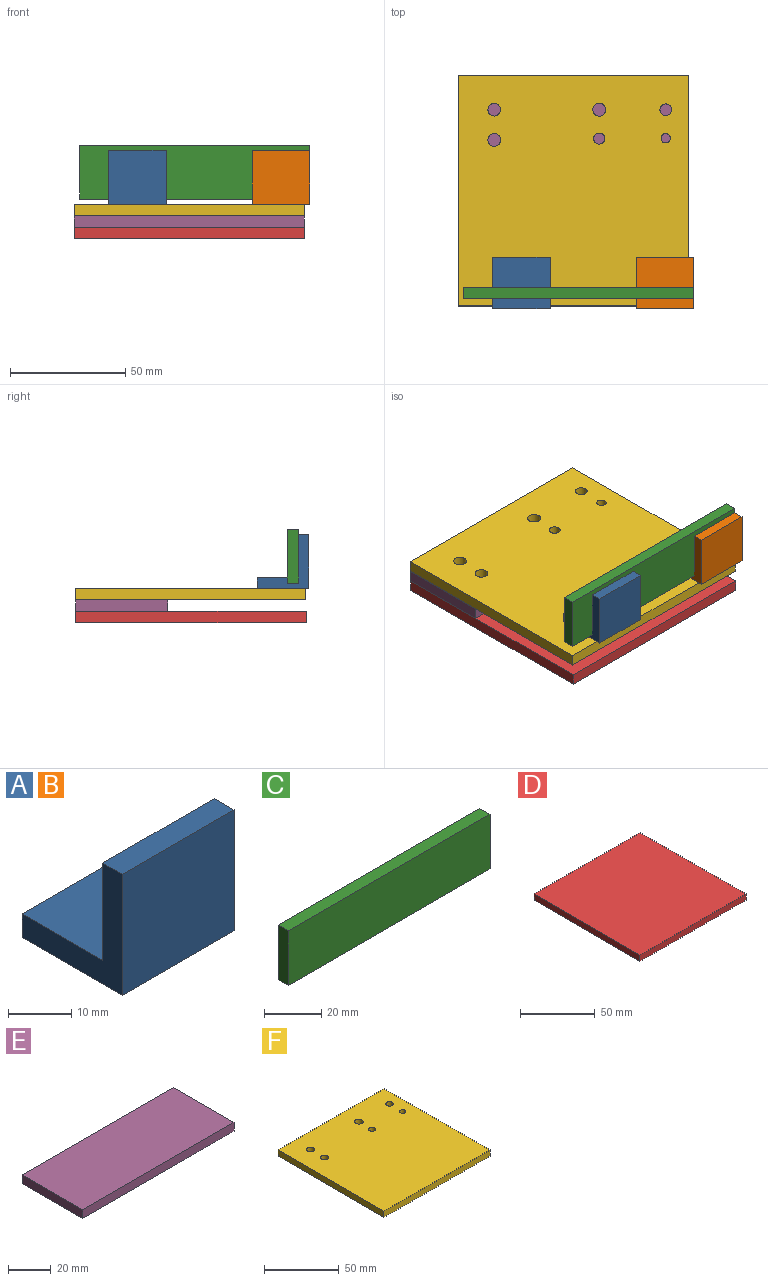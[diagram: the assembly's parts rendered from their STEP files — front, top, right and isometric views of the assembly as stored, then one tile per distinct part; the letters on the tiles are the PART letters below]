
ASSEMBLY  parts=6 mates=5
PART A: 8 faces, bbox 25x22.5x23.5 mm
  f0: plane 25x4.41mm, normal (0,0,1), area 110.2mm2, adj f1,f5,f6,f7
  f1: plane 25x23.47mm, normal (0,-1,0), area 586.8mm2, adj f0,f2,f6,f7
  f2: plane 25x22.48mm, normal (0,0,-1), area 562.1mm2, adj f1,f3,f6,f7
  f3: plane 25x4.58mm, normal (0,1,0), area 114.5mm2, adj f2,f4,f6,f7
  f4: plane 25x18.08mm, normal (0,0,1), area 451.9mm2, adj f3,f5,f6,f7
  f5: plane 25x18.89mm, normal (0,1,0), area 472.3mm2, adj f0,f4,f6,f7
  f6: plane 23.47x22.48mm, normal (1,0,0), area 186.2mm2, adj f0,f1,f2,f3,f4,f5
  f7: plane 23.47x22.48mm, normal (-1,0,0), area 186.2mm2, adj f0,f1,f2,f3,f4,f5
PART B: same geometry as A
PART C: 6 faces, bbox 100x5x23.5 mm
  f0: plane 100x5mm, normal (0,0,1), area 500mm2, adj f1,f3,f4,f5
  f1: plane 100x23.47mm, normal (0,-1,0), area 2347.2mm2, adj f0,f2,f4,f5
  f2: plane 100x5mm, normal (0,0,-1), area 500mm2, adj f1,f3,f4,f5
  f3: plane 100x23.47mm, normal (0,1,0), area 2347.2mm2, adj f0,f2,f4,f5
  f4: plane 23.47x5mm, normal (1,0,0), area 117.4mm2, adj f0,f1,f2,f3
  f5: plane 23.47x5mm, normal (-1,0,0), area 117.4mm2, adj f0,f1,f2,f3
PART D: 6 faces, bbox 100x100x5 mm
  f0: plane 100x100mm, normal (0,0,1), area 10000mm2, adj f1,f3,f4,f5
  f1: plane 100x5mm, normal (0,-1,0), area 500mm2, adj f0,f2,f4,f5
  f2: plane 100x100mm, normal (0,0,-1), area 10000mm2, adj f1,f3,f4,f5
  f3: plane 100x5mm, normal (0,1,0), area 500mm2, adj f0,f2,f4,f5
  f4: plane 100x5mm, normal (1,0,0), area 500mm2, adj f0,f1,f2,f3
  f5: plane 100x5mm, normal (-1,0,0), area 500mm2, adj f0,f1,f2,f3
PART E: 6 faces, bbox 100x40x5 mm
  f0: plane 100x40mm, normal (0,0,1), area 4000mm2, adj f1,f3,f4,f5
  f1: plane 100x5mm, normal (0,-1,0), area 500mm2, adj f0,f2,f4,f5
  f2: plane 100x40mm, normal (0,0,-1), area 4000mm2, adj f1,f3,f4,f5
  f3: plane 100x5mm, normal (0,1,0), area 500mm2, adj f0,f2,f4,f5
  f4: plane 40x5mm, normal (1,0,0), area 200mm2, adj f0,f1,f2,f3
  f5: plane 40x5mm, normal (-1,0,0), area 200mm2, adj f0,f1,f2,f3
PART F: 12 faces, bbox 100x100x5 mm
  f0: plane 100x100mm, normal (0,0,1), area 9876mm2, adj f1,f3,f4,f5,f6,f7,f8,f9
  f1: plane 100x5mm, normal (0,-1,0), area 500mm2, adj f0,f2,f4,f5
  f2: plane 100x100mm, normal (0,0,-1), area 9876mm2, adj f1,f3,f4,f5,f6,f7,f8,f9
  f3: plane 100x5mm, normal (0,1,0), area 500mm2, adj f0,f2,f4,f5
  f4: plane 100x5mm, normal (1,0,0), area 500mm2, adj f0,f1,f2,f3
  f5: plane 100x5mm, normal (-1,0,0), area 500mm2, adj f0,f1,f2,f3
  f6: cylinder r=2.06mm len=5mm, axis (0,0,1), area 64.7mm2, adj f0,f2
  f7: cylinder r=2.76mm len=5.52mm, axis (0,0,1), area 86.7mm2, adj f0,f2
  f8: cylinder r=2.51mm len=5.02mm, axis (0,0,1), area 78.8mm2, adj f0,f2
  f9: cylinder r=2.39mm len=5mm, axis (0,0,1), area 75.1mm2, adj f0,f2
  f10: cylinder r=2.77mm len=5.54mm, axis (0,0,1), area 87.1mm2, adj f0,f2
  f11: cylinder r=2.81mm len=5.63mm, axis (0,0,1), area 88.4mm2, adj f0,f2
PLACE A t=(14.98,-0.99,81.72)mm
PLACE B t=(77.48,-0.99,81.72)mm
PLACE C t=(2.48,-41.84,84.01)mm
PLACE D t=(-0.02,-0.37,2.06)mm
PLACE E t=(-0.02,-0.37,0.88)mm
PLACE F at identity
MATE fastened E.f0 <-> F.f2  axis (0,0,1) through (49.98,39.76,32.11)mm
MATE fastened A.f2 <-> F.f0  axis (0,0,-1) through (39.98,-30.24,37.11)mm
MATE fastened C.f1 <-> A.f5  axis (0,-1,0) through (52.48,-37.07,51.14)mm
MATE fastened D.f0 <-> E.f2  axis (0,0,1) through (49.98,59.76,27.11)mm
MATE fastened B.f2 <-> F.f0  axis (0,0,-1) through (89.98,-30.24,37.11)mm
